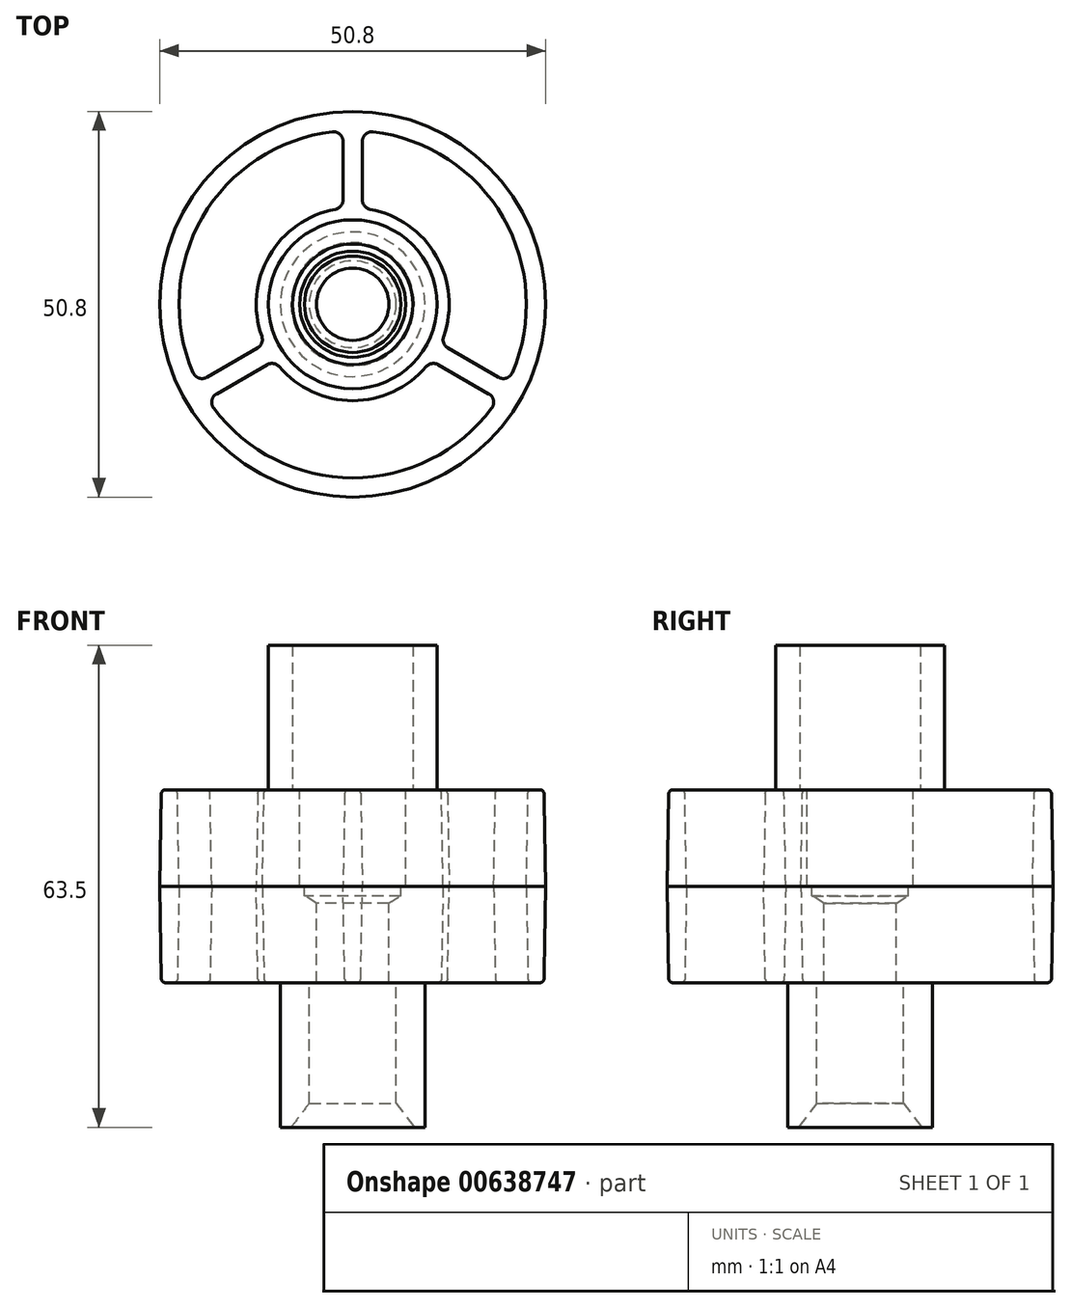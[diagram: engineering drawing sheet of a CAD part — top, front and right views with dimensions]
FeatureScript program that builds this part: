
annotation { "Feature Type Name" : "Feature", "Feature Type Description" : "" }
export const myFeature = defineFeature(function(context is Context, id is Id, definition is map)
    precondition{}
    {
        {
            var Q0;
            Q0=qCreatedBy(makeId("Top.planeOp"),FACE);
            var sketch = newSketch(context, id + "F0", { "sketchPlane" : qUnion([Q0])});
            skArc(sketch, "E0", {"start": v(11.97, -4.24) * mm, "mid": v(11, 6.35) * mm, "end": v(2.3, 12.49) * mm});
            skCircle(sketch, "E1", {"center": v(0, 0) * mm, "radius": 25.4 * mm});
            skArc(sketch, "E2", {"start": v(-18.32, -13.68) * mm, "mid": v(0, -22.86) * mm, "end": v(18.32, -13.68) * mm});
            skLineSegment(sketch, "E3", {"start": v(-1.27, 21.44) * mm, "end": v(-1.27, 13.74) * mm});
            skLineSegment(sketch, "E4", {"start": v(1.27, 21.44) * mm, "end": v(1.27, 13.74) * mm});
            skLineSegment(sketch, "E5.1.0", {"start": v(-17.93, -11.82) * mm, "end": v(-11.26, -7.97) * mm});
            skLineSegment(sketch, "E5.1.1", {"start": v(-19.2, -9.62) * mm, "end": v(-12.53, -5.77) * mm});
            skLineSegment(sketch, "E5.2.0", {"start": v(19.2, -9.62) * mm, "end": v(12.53, -5.77) * mm});
            skLineSegment(sketch, "E5.2.1", {"start": v(17.93, -11.82) * mm, "end": v(11.26, -7.97) * mm});
            skArc(sketch, "E6.trimOffspring", {"start": v(-2.3, 12.49) * mm, "mid": v(-11, 6.35) * mm, "end": v(-11.97, -4.24) * mm});
            skArc(sketch, "E7.trimOffspring", {"start": v(-9.66, -8.24) * mm, "mid": v(0, -12.7) * mm, "end": v(9.66, -8.24) * mm});
            skArc(sketch, "E8.trimOffspring", {"start": v(-2.69, 22.7) * mm, "mid": v(-19.8, 11.43) * mm, "end": v(-21, -9.02) * mm});
            skArc(sketch, "E9.trimOffspring", {"start": v(21, -9.02) * mm, "mid": v(19.8, 11.43) * mm, "end": v(2.69, 22.7) * mm});
            skPoint(sketch, "E10.orphan", {"position": v(10.51, -4.6) * mm});
            skPoint(sketch, "E11.orphan", {"position": v(9.24, -6.8) * mm});
            skPoint(sketch, "E12.orphan", {"position": v(19.88, -12.94) * mm});
            skPoint(sketch, "E13.orphan", {"position": v(21.15, -10.74) * mm});
            skPoint(sketch, "E14.orphan", {"position": v(-9.24, -6.8) * mm});
            skPoint(sketch, "E15.orphan", {"position": v(-10.51, -4.6) * mm});
            skPoint(sketch, "E16.orphan", {"position": v(-21.15, -10.74) * mm});
            skPoint(sketch, "E17.orphan", {"position": v(-19.88, -12.94) * mm});
            skPoint(sketch, "E18.orphan", {"position": v(-1.27, 11.4) * mm});
            skPoint(sketch, "E19.orphan", {"position": v(1.27, 11.4) * mm});
            skPoint(sketch, "E20.orphan", {"position": v(1.27, 23.68) * mm});
            skPoint(sketch, "E21.orphan", {"position": v(-1.27, 23.68) * mm});
            skPoint(sketch, "E22.visualSharp", {"position": v(-20.4, -10.31) * mm});
            skArc(sketch, "E22.filletArc", {"start": v(-21, -9.02) * mm, "mid": v(-20.24, -9.73) * mm, "end": v(-19.2, -9.62) * mm});
            skPoint(sketch, "E23.visualSharp", {"position": v(-19.13, -12.51) * mm});
            skArc(sketch, "E23.filletArc", {"start": v(-17.93, -11.82) * mm, "mid": v(-18.54, -12.66) * mm, "end": v(-18.32, -13.68) * mm});
            skPoint(sketch, "E24.visualSharp", {"position": v(19.13, -12.51) * mm});
            skArc(sketch, "E24.filletArc", {"start": v(18.32, -13.68) * mm, "mid": v(18.54, -12.66) * mm, "end": v(17.93, -11.82) * mm});
            skPoint(sketch, "E25.visualSharp", {"position": v(20.4, -10.31) * mm});
            skArc(sketch, "E25.filletArc", {"start": v(19.2, -9.62) * mm, "mid": v(20.24, -9.73) * mm, "end": v(21, -9.02) * mm});
            skPoint(sketch, "E26.visualSharp", {"position": v(1.27, 22.82) * mm});
            skArc(sketch, "E26.filletArc", {"start": v(2.69, 22.7) * mm, "mid": v(1.7, 22.39) * mm, "end": v(1.27, 21.44) * mm});
            skPoint(sketch, "E27.visualSharp", {"position": v(-1.27, 22.82) * mm});
            skArc(sketch, "E27.filletArc", {"start": v(-1.27, 21.44) * mm, "mid": v(-1.7, 22.39) * mm, "end": v(-2.69, 22.7) * mm});
            skPoint(sketch, "E28.visualSharp", {"position": v(-1.27, 12.64) * mm});
            skArc(sketch, "E28.filletArc", {"start": v(-2.3, 12.49) * mm, "mid": v(-1.56, 12.92) * mm, "end": v(-1.27, 13.74) * mm});
            skPoint(sketch, "E29.visualSharp", {"position": v(1.27, 12.64) * mm});
            skArc(sketch, "E29.filletArc", {"start": v(1.27, 13.74) * mm, "mid": v(1.56, 12.92) * mm, "end": v(2.3, 12.49) * mm});
            skPoint(sketch, "E30.visualSharp", {"position": v(-11.58, -5.22) * mm});
            skArc(sketch, "E30.filletArc", {"start": v(-12.53, -5.77) * mm, "mid": v(-11.98, -5.1) * mm, "end": v(-11.97, -4.24) * mm});
            skPoint(sketch, "E31.visualSharp", {"position": v(-10.3, -7.42) * mm});
            skArc(sketch, "E31.filletArc", {"start": v(-9.66, -8.24) * mm, "mid": v(-10.41, -7.82) * mm, "end": v(-11.26, -7.97) * mm});
            skPoint(sketch, "E32.visualSharp", {"position": v(10.3, -7.42) * mm});
            skArc(sketch, "E32.filletArc", {"start": v(11.26, -7.97) * mm, "mid": v(10.41, -7.82) * mm, "end": v(9.66, -8.24) * mm});
            skPoint(sketch, "E33.visualSharp", {"position": v(11.58, -5.22) * mm});
            skArc(sketch, "E33.filletArc", {"start": v(11.97, -4.24) * mm, "mid": v(11.98, -5.1) * mm, "end": v(12.53, -5.77) * mm});
            skSolve(sketch);
        }
        {
            var Q0;
            Q0=makeQuery(id+"F0.imprint","IMPRINT",FACE,{"disambiguationData":[TD([[makeQuery(id+"F0.imprint","IMPRINT",EDGE,{"derivedFrom":sQuery(id+"F0.wireOp",EDGE,"E0")}),1.0]])]});
            extrude(context, id + "F1", {"entities" : qUnion([Q0]), "endBound" : BoundingType.SYMMETRIC, "depth" : 25.4 * mm, "offsetDistance" : 25.4 * mm, "hasDraft" : true, "draftAngle" : 1 * degree, "draftPullDirection" : true});
        }
        {
            var Q0;
            Q0=makeQuery(id+"F1.opExtrude","CAP_FACE",FACE,{"disambiguationData":[OSD([sQuery(id+"F0.wireOp",EDGE,"E0"),sQuery(id+"F0.wireOp",EDGE,"E1"),sQuery(id+"F0.wireOp",EDGE,"E2"),sQuery(id+"F0.wireOp",EDGE,"E3"),sQuery(id+"F0.wireOp",EDGE,"E4"),sQuery(id+"F0.wireOp",EDGE,"E5.1.0"),sQuery(id+"F0.wireOp",EDGE,"E5.1.1"),sQuery(id+"F0.wireOp",EDGE,"E5.2.0"),sQuery(id+"F0.wireOp",EDGE,"E5.2.1"),sQuery(id+"F0.wireOp",EDGE,"E6.trimOffspring"),sQuery(id+"F0.wireOp",EDGE,"E7.trimOffspring"),sQuery(id+"F0.wireOp",EDGE,"E8.trimOffspring"),sQuery(id+"F0.wireOp",EDGE,"E9.trimOffspring"),sQuery(id+"F0.wireOp",EDGE,"E22.filletArc"),sQuery(id+"F0.wireOp",EDGE,"E23.filletArc"),sQuery(id+"F0.wireOp",EDGE,"E24.filletArc"),sQuery(id+"F0.wireOp",EDGE,"E25.filletArc"),sQuery(id+"F0.wireOp",EDGE,"E26.filletArc"),sQuery(id+"F0.wireOp",EDGE,"E27.filletArc"),sQuery(id+"F0.wireOp",EDGE,"E28.filletArc"),sQuery(id+"F0.wireOp",EDGE,"E29.filletArc"),sQuery(id+"F0.wireOp",EDGE,"E30.filletArc"),sQuery(id+"F0.wireOp",EDGE,"E31.filletArc"),sQuery(id+"F0.wireOp",EDGE,"E32.filletArc"),sQuery(id+"F0.wireOp",EDGE,"E33.filletArc"),sQuery(id+"F0.wireOp",EDGE,"ev8RRVpv-P6tY-glvH-UhQw-a3gVWC9BexQm")])],"isStart":false});
            var Q1;
            Q1=makeQuery(id+"F1.opExtrude","CAP_FACE",FACE,{"disambiguationData":[OSD([sQuery(id+"F0.wireOp",EDGE,"E0"),sQuery(id+"F0.wireOp",EDGE,"E1"),sQuery(id+"F0.wireOp",EDGE,"E2"),sQuery(id+"F0.wireOp",EDGE,"E3"),sQuery(id+"F0.wireOp",EDGE,"E4"),sQuery(id+"F0.wireOp",EDGE,"E5.1.0"),sQuery(id+"F0.wireOp",EDGE,"E5.1.1"),sQuery(id+"F0.wireOp",EDGE,"E5.2.0"),sQuery(id+"F0.wireOp",EDGE,"E5.2.1"),sQuery(id+"F0.wireOp",EDGE,"E6.trimOffspring"),sQuery(id+"F0.wireOp",EDGE,"E7.trimOffspring"),sQuery(id+"F0.wireOp",EDGE,"E8.trimOffspring"),sQuery(id+"F0.wireOp",EDGE,"E9.trimOffspring"),sQuery(id+"F0.wireOp",EDGE,"E22.filletArc"),sQuery(id+"F0.wireOp",EDGE,"E23.filletArc"),sQuery(id+"F0.wireOp",EDGE,"E24.filletArc"),sQuery(id+"F0.wireOp",EDGE,"E25.filletArc"),sQuery(id+"F0.wireOp",EDGE,"E26.filletArc"),sQuery(id+"F0.wireOp",EDGE,"E27.filletArc"),sQuery(id+"F0.wireOp",EDGE,"E28.filletArc"),sQuery(id+"F0.wireOp",EDGE,"E29.filletArc"),sQuery(id+"F0.wireOp",EDGE,"E30.filletArc"),sQuery(id+"F0.wireOp",EDGE,"E31.filletArc"),sQuery(id+"F0.wireOp",EDGE,"E32.filletArc"),sQuery(id+"F0.wireOp",EDGE,"E33.filletArc"),sQuery(id+"F0.wireOp",EDGE,"ev8RRVpv-P6tY-glvH-UhQw-a3gVWC9BexQm")])],"isStart":true});
            fillet(context, id + "F2", {"entities" : qUnion([Q0, Q1]), "radius" : 0.5 * mm, "tangentPropagation" : true, "allowEdgeOverflow" : false});
        }
        {
            var Q0;
            Q0=makeQuery(id+"F1.opExtrude","CAP_FACE",FACE,{"disambiguationData":[OSD([sQuery(id+"F0.wireOp",EDGE,"E0"),sQuery(id+"F0.wireOp",EDGE,"E1"),sQuery(id+"F0.wireOp",EDGE,"E2"),sQuery(id+"F0.wireOp",EDGE,"E3"),sQuery(id+"F0.wireOp",EDGE,"E4"),sQuery(id+"F0.wireOp",EDGE,"E5.1.0"),sQuery(id+"F0.wireOp",EDGE,"E5.1.1"),sQuery(id+"F0.wireOp",EDGE,"E5.2.0"),sQuery(id+"F0.wireOp",EDGE,"E5.2.1"),sQuery(id+"F0.wireOp",EDGE,"E6.trimOffspring"),sQuery(id+"F0.wireOp",EDGE,"E7.trimOffspring"),sQuery(id+"F0.wireOp",EDGE,"E8.trimOffspring"),sQuery(id+"F0.wireOp",EDGE,"E9.trimOffspring"),sQuery(id+"F0.wireOp",EDGE,"E22.filletArc"),sQuery(id+"F0.wireOp",EDGE,"E23.filletArc"),sQuery(id+"F0.wireOp",EDGE,"E24.filletArc"),sQuery(id+"F0.wireOp",EDGE,"E25.filletArc"),sQuery(id+"F0.wireOp",EDGE,"E26.filletArc"),sQuery(id+"F0.wireOp",EDGE,"E27.filletArc"),sQuery(id+"F0.wireOp",EDGE,"E28.filletArc"),sQuery(id+"F0.wireOp",EDGE,"E29.filletArc"),sQuery(id+"F0.wireOp",EDGE,"E30.filletArc"),sQuery(id+"F0.wireOp",EDGE,"E31.filletArc"),sQuery(id+"F0.wireOp",EDGE,"E32.filletArc"),sQuery(id+"F0.wireOp",EDGE,"E33.filletArc")])],"isStart":false});
            var sketch = newSketch(context, id + "F3", { "sketchPlane" : qUnion([Q0])});
            skCircle(sketch, "E34", {"center": v(0, 0) * mm, "radius": 11.11 * mm});
            skCircle(sketch, "E35", {"center": v(0, 0) * mm, "radius": 7.94 * mm});
            skSolve(sketch);
        }
        {
            var Q0;
            Q0=makeQuery(id+"F3.imprint","IMPRINT",FACE,{"disambiguationData":[TD([[makeQuery(id+"F3.imprint","IMPRINT",EDGE,{"derivedFrom":sQuery(id+"F3.wireOp",EDGE,"E34")}),1.0]])]});
            extrude(context, id + "F4", {"entities" : qUnion([Q0]), "operationType" : NewBodyOperationType.ADD, "depth" : 19.05 * mm, "offsetDistance" : 25.4 * mm});
        }
        {
            var Q0;
            Q0=sQuery(id+"F3.wireOp",VERTEX,"E34.center");
            var Q1;
            Q1=makeQuery(id+"F1.opExtrude","SWEPT_BODY",BODY,{"disambiguationData":[OSD([sQuery(id+"F0.wireOp",EDGE,"E0"),sQuery(id+"F0.wireOp",EDGE,"E1"),sQuery(id+"F0.wireOp",EDGE,"E2"),sQuery(id+"F0.wireOp",EDGE,"E3"),sQuery(id+"F0.wireOp",EDGE,"E4"),sQuery(id+"F0.wireOp",EDGE,"E5.1.0"),sQuery(id+"F0.wireOp",EDGE,"E5.1.1"),sQuery(id+"F0.wireOp",EDGE,"E5.2.0"),sQuery(id+"F0.wireOp",EDGE,"E5.2.1"),sQuery(id+"F0.wireOp",EDGE,"E6.trimOffspring"),sQuery(id+"F0.wireOp",EDGE,"E7.trimOffspring"),sQuery(id+"F0.wireOp",EDGE,"E8.trimOffspring"),sQuery(id+"F0.wireOp",EDGE,"E9.trimOffspring"),sQuery(id+"F0.wireOp",EDGE,"E22.filletArc"),sQuery(id+"F0.wireOp",EDGE,"E23.filletArc"),sQuery(id+"F0.wireOp",EDGE,"E24.filletArc"),sQuery(id+"F0.wireOp",EDGE,"E25.filletArc"),sQuery(id+"F0.wireOp",EDGE,"E26.filletArc"),sQuery(id+"F0.wireOp",EDGE,"E27.filletArc"),sQuery(id+"F0.wireOp",EDGE,"E28.filletArc"),sQuery(id+"F0.wireOp",EDGE,"E29.filletArc"),sQuery(id+"F0.wireOp",EDGE,"E30.filletArc"),sQuery(id+"F0.wireOp",EDGE,"E31.filletArc"),sQuery(id+"F0.wireOp",EDGE,"E32.filletArc"),sQuery(id+"F0.wireOp",EDGE,"E33.filletArc")])]});
            hole(context, id + "F5", {"style" : HoleStyle.C_BORE, "endStyle" : HoleEndStyle.THROUGH, "holeDiameter" : 9.52 * mm, "cBoreDiameter" : 13.97 * mm, "cBoreDepth" : 12.7 * mm, "majorDiameter" : 6.35 * mm, "isTappedThrough" : true, "tappedDepth" : 12.7 * mm, "tapClearance" : 3, "startFromSketch" : true, "locations" : qUnion([Q0]), "scope" : qUnion([Q1])});
        }
        {
            var Q0;
            Q0=qCreatedBy(makeId("Top.planeOp"),FACE);
            var sketch = newSketch(context, id + "F6", { "sketchPlane" : qUnion([Q0])});
            skPoint(sketch, "E36", {"position": v(0, 0) * mm});
            skSolve(sketch);
        }
        {
            var Q0;
            Q0=sQuery(id+"F6.wireOp",VERTEX,"E36");
            var Q1;
            Q1=makeQuery(id+"F1.opExtrude","SWEPT_BODY",BODY,{"disambiguationData":[OSD([sQuery(id+"F0.wireOp",EDGE,"E0"),sQuery(id+"F0.wireOp",EDGE,"E1"),sQuery(id+"F0.wireOp",EDGE,"E2"),sQuery(id+"F0.wireOp",EDGE,"E3"),sQuery(id+"F0.wireOp",EDGE,"E4"),sQuery(id+"F0.wireOp",EDGE,"E5.1.0"),sQuery(id+"F0.wireOp",EDGE,"E5.1.1"),sQuery(id+"F0.wireOp",EDGE,"E5.2.0"),sQuery(id+"F0.wireOp",EDGE,"E5.2.1"),sQuery(id+"F0.wireOp",EDGE,"E6.trimOffspring"),sQuery(id+"F0.wireOp",EDGE,"E7.trimOffspring"),sQuery(id+"F0.wireOp",EDGE,"E8.trimOffspring"),sQuery(id+"F0.wireOp",EDGE,"E9.trimOffspring"),sQuery(id+"F0.wireOp",EDGE,"E22.filletArc"),sQuery(id+"F0.wireOp",EDGE,"E23.filletArc"),sQuery(id+"F0.wireOp",EDGE,"E24.filletArc"),sQuery(id+"F0.wireOp",EDGE,"E25.filletArc"),sQuery(id+"F0.wireOp",EDGE,"E26.filletArc"),sQuery(id+"F0.wireOp",EDGE,"E27.filletArc"),sQuery(id+"F0.wireOp",EDGE,"E28.filletArc"),sQuery(id+"F0.wireOp",EDGE,"E29.filletArc"),sQuery(id+"F0.wireOp",EDGE,"E30.filletArc"),sQuery(id+"F0.wireOp",EDGE,"E31.filletArc"),sQuery(id+"F0.wireOp",EDGE,"E32.filletArc"),sQuery(id+"F0.wireOp",EDGE,"E33.filletArc")])]});
            hole(context, id + "F7", {"style" : HoleStyle.SIMPLE, "endStyle" : HoleEndStyle.BLIND, "holeDiameter" : 12.7 * mm, "majorDiameter" : 6.35 * mm, "holeDepth" : 1.27 * mm, "isTappedThrough" : true, "tappedDepth" : 12.7 * mm, "tapClearance" : 3, "startFromSketch" : true, "locations" : qUnion([Q0]), "scope" : qUnion([Q1])});
        }
        {
            var Q0;
            Q0=makeQuery(id+"F1.opExtrude","CAP_FACE",FACE,{"disambiguationData":[OSD([sQuery(id+"F0.wireOp",EDGE,"E0"),sQuery(id+"F0.wireOp",EDGE,"E1"),sQuery(id+"F0.wireOp",EDGE,"E2"),sQuery(id+"F0.wireOp",EDGE,"E3"),sQuery(id+"F0.wireOp",EDGE,"E4"),sQuery(id+"F0.wireOp",EDGE,"E5.1.0"),sQuery(id+"F0.wireOp",EDGE,"E5.1.1"),sQuery(id+"F0.wireOp",EDGE,"E5.2.0"),sQuery(id+"F0.wireOp",EDGE,"E5.2.1"),sQuery(id+"F0.wireOp",EDGE,"E6.trimOffspring"),sQuery(id+"F0.wireOp",EDGE,"E7.trimOffspring"),sQuery(id+"F0.wireOp",EDGE,"E8.trimOffspring"),sQuery(id+"F0.wireOp",EDGE,"E9.trimOffspring"),sQuery(id+"F0.wireOp",EDGE,"E22.filletArc"),sQuery(id+"F0.wireOp",EDGE,"E23.filletArc"),sQuery(id+"F0.wireOp",EDGE,"E24.filletArc"),sQuery(id+"F0.wireOp",EDGE,"E25.filletArc"),sQuery(id+"F0.wireOp",EDGE,"E26.filletArc"),sQuery(id+"F0.wireOp",EDGE,"E27.filletArc"),sQuery(id+"F0.wireOp",EDGE,"E28.filletArc"),sQuery(id+"F0.wireOp",EDGE,"E29.filletArc"),sQuery(id+"F0.wireOp",EDGE,"E30.filletArc"),sQuery(id+"F0.wireOp",EDGE,"E31.filletArc"),sQuery(id+"F0.wireOp",EDGE,"E32.filletArc"),sQuery(id+"F0.wireOp",EDGE,"E33.filletArc")])],"isStart":true});
            var sketch = newSketch(context, id + "F8", { "sketchPlane" : qUnion([Q0])});
            skPoint(sketch, "E37", {"position": v(0, 0) * mm});
            skCircle(sketch, "E38", {"center": v(0, 0) * mm, "radius": 9.53 * mm});
            skCircle(sketch, "E39", {"center": v(0, 0) * mm, "radius": 5.72 * mm});
            skSolve(sketch);
        }
        {
            var Q0;
            Q0=makeQuery(id+"F8.imprint","IMPRINT",FACE,{"disambiguationData":[TD([[makeQuery(id+"F8.imprint","IMPRINT",EDGE,{"derivedFrom":sQuery(id+"F8.wireOp",EDGE,"E38")}),1.0]])]});
            extrude(context, id + "F9", {"entities" : qUnion([Q0]), "operationType" : NewBodyOperationType.ADD, "depth" : 19.05 * mm, "offsetDistance" : 25.4 * mm});
        }
        {
            var Q0;
            Q0=makeQuery(id+"F9.opExtrude","CAP_EDGE",EDGE,{"disambiguationData":[OSD([sQuery(id+"F8.wireOp",EDGE,"E39")])],"isStart":false});
            chamfer(context, id + "F10", {"entities" : qUnion([Q0]), "chamferType" : ChamferType.OFFSET_ANGLE, "width" : 3.17 * mm, "oppositeDirection" : false, "angle" : 37 * degree, "tangentPropagation" : true});
        }
    });
